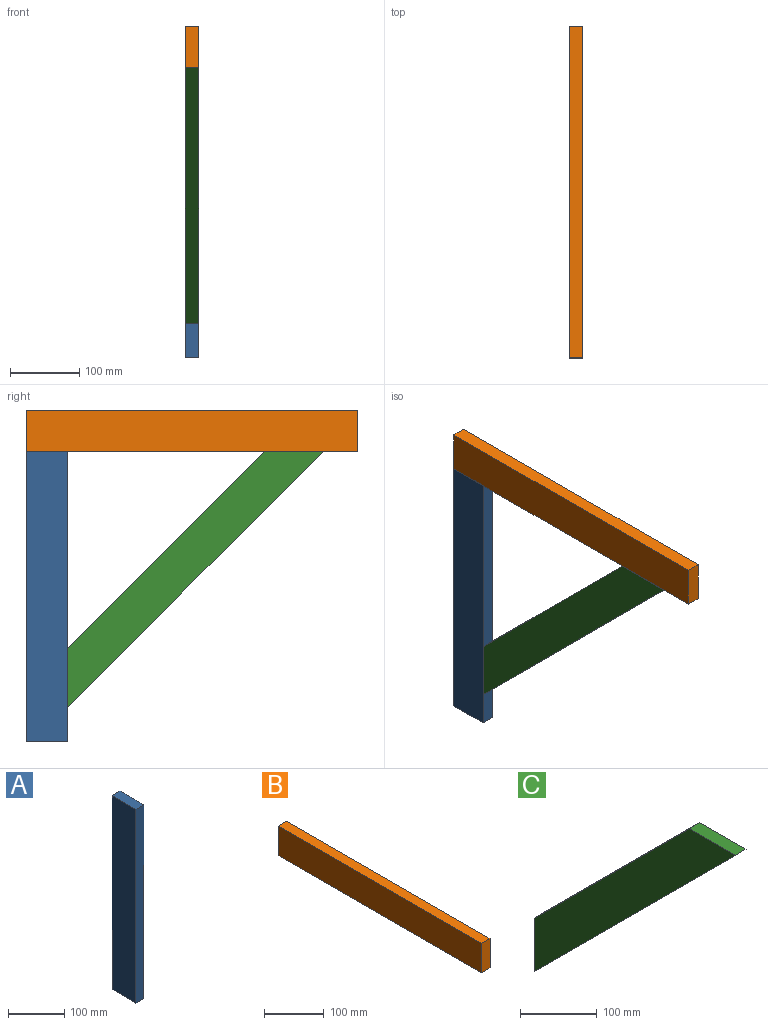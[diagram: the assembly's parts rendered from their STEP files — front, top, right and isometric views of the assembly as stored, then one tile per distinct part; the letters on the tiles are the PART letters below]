
ASSEMBLY  parts=3 mates=6
PART A: 6 faces, bbox 20x60x420 mm
  f0: plane 60x20mm, normal (0,0,1), area 1200mm2, adj f1,f3,f4,f5
  f1: plane 420x20mm, normal (0,1,0), area 8400mm2, adj f0,f2,f4,f5
  f2: plane 60x20mm, normal (0,0,-1), area 1200mm2, adj f1,f3,f4,f5
  f3: plane 420x20mm, normal (0,-1,0), area 8400mm2, adj f0,f2,f4,f5
  f4: plane 420x60mm, normal (1,0,0), area 25200mm2, adj f0,f1,f2,f3
  f5: plane 420x60mm, normal (-1,0,0), area 25200mm2, adj f0,f1,f2,f3
PART B: 6 faces, bbox 20x480x60 mm
  f0: plane 60x20mm, normal (0,1,0), area 1200mm2, adj f1,f3,f4,f5
  f1: plane 480x20mm, normal (0,0,1), area 9600mm2, adj f0,f2,f4,f5
  f2: plane 60x20mm, normal (0,-1,0), area 1200mm2, adj f1,f3,f4,f5
  f3: plane 480x20mm, normal (0,0,-1), area 9600mm2, adj f0,f2,f4,f5
  f4: plane 480x60mm, normal (1,0,0), area 28800mm2, adj f0,f1,f2,f3
  f5: plane 480x60mm, normal (-1,0,0), area 28800mm2, adj f0,f1,f2,f3
PART C: 6 faces, bbox 20x370x370 mm
  f0: plane 370x370mm, normal (0,-0.71,-0.71), area 10465.2mm2, adj f1,f3,f4,f5
  f1: plane 84.85x20mm, normal (0,0,1), area 1697.1mm2, adj f0,f2,f4,f5
  f2: plane 285.15x285.15mm, normal (0,0.71,0.71), area 8065.2mm2, adj f1,f3,f4,f5
  f3: plane 84.85x20mm, normal (0,1,0), area 1697.1mm2, adj f0,f2,f4,f5
  f4: plane 370x370mm, normal (1,0,0), area 27795.5mm2, adj f0,f1,f2,f3
  f5: plane 370x370mm, normal (-1,0,0), area 27795.5mm2, adj f0,f1,f2,f3
PLACE A t=(0,20,20)mm
PLACE B t=(0,20,20)mm fixed
PLACE C t=(0,20,20)mm
MATE planar A.f3 <-> C.f3  axis (0,-1,0) through (0,-60,-280)mm
MATE planar B.f0 <-> A.f1  axis (0,1,0) through (0,0,-40)mm
MATE planar A.f5 <-> C.f5  axis (-1,0,0) through (-10,-30,-280)mm
MATE planar B.f5 <-> A.f5  axis (-1,0,0) through (-10,-240,-40)mm
MATE planar B.f3 <-> C.f1  axis (0,0,-1) through (0,-240,-70)mm
MATE planar A.f0 <-> B.f3  axis (0,0,1) through (0,-30,-70)mm
